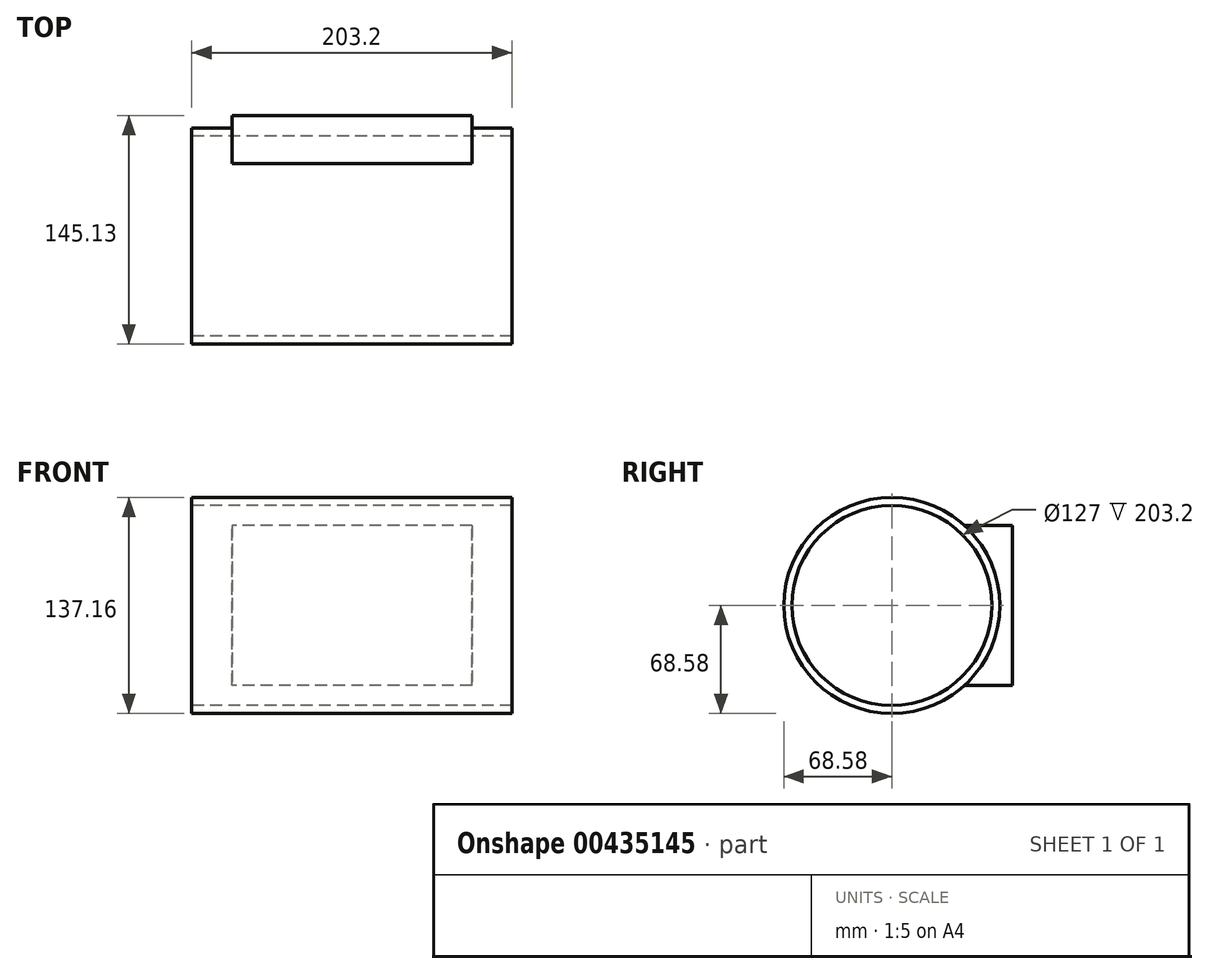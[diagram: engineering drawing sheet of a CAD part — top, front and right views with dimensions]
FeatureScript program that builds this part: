
annotation { "Feature Type Name" : "Feature", "Feature Type Description" : "" }
export const myFeature = defineFeature(function(context is Context, id is Id, definition is map)
    precondition{}
    {
        {
            var Q0;
            Q0=qCreatedBy(makeId("Right.planeOp"),FACE);
            var sketch = newSketch(context, id + "F0", { "sketchPlane" : qUnion([Q0])});
            skCircle(sketch, "E0", {"center": v(0, 0) * mm, "radius": 63.5 * mm});
            skCircle(sketch, "E1", {"center": v(0, 0) * mm, "radius": 68.58 * mm});
            skLineSegment(sketch, "E2", {"start": v(46.07, 50.8) * mm, "end": v(76.55, 50.8) * mm});
            skLineSegment(sketch, "E3", {"start": v(76.55, 50.8) * mm, "end": v(76.55, 0) * mm});
            skLineSegment(sketch, "E4.MirrorCS", {"start": v(46.07, -50.8) * mm, "end": v(76.55, -50.8) * mm});
            skLineSegment(sketch, "E5.MirrorCS", {"start": v(76.55, -50.8) * mm, "end": v(76.55, 0) * mm});
            skSolve(sketch);
        }
        {
            var Q0;
            Q0=makeQuery(id+"F0.imprint","IMPRINT",FACE,{"disambiguationData":[TD([[makeQuery(id+"F0.imprint","IMPRINT",EDGE,{"derivedFrom":sQuery(id+"F0.wireOp",EDGE,"E0")}),-1.0]])]});
            extrude(context, id + "F1", {"entities" : qUnion([Q0]), "endBound" : BoundingType.SYMMETRIC, "depth" : 203.2 * mm});
        }
        {
            var Q0;
            {var subQ1=sQuery(id+"F0.wireOp",EDGE,"E2");Q0=makeQuery(id+"F0.imprint","IMPRINT",FACE,{"disambiguationData":[TD([[makeQuery(id+"F0.imprint","IMPRINT",EDGE,{"derivedFrom":subQ1}),-1.0]])]});}
            extrude(context, id + "F2", {"entities" : qUnion([Q0]), "operationType" : NewBodyOperationType.ADD, "endBound" : BoundingType.SYMMETRIC, "depth" : 152.4 * mm});
        }
    });
